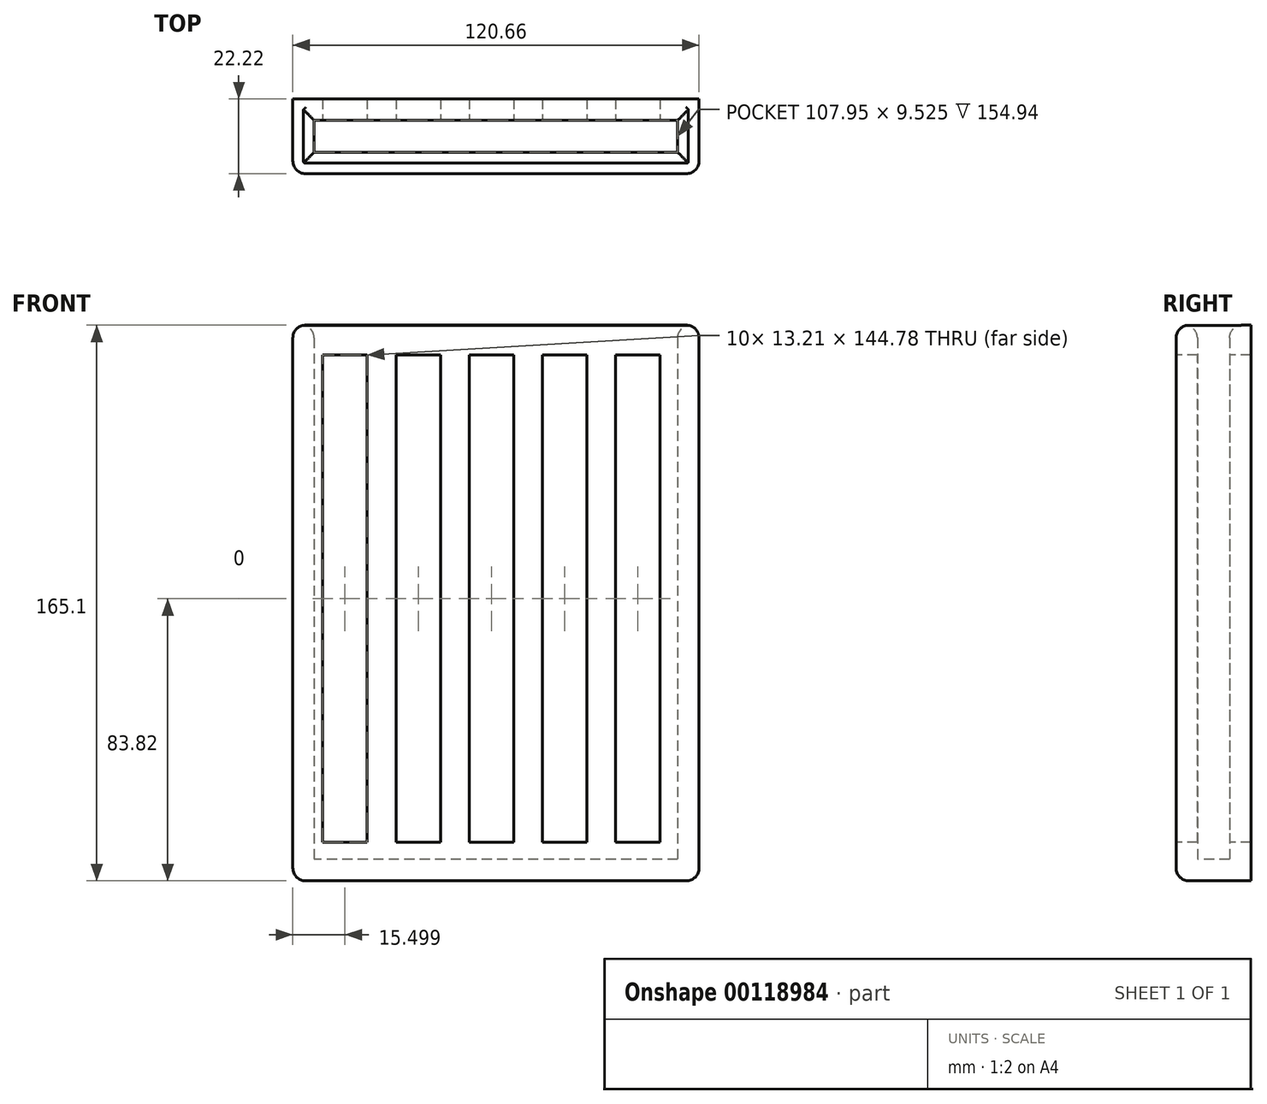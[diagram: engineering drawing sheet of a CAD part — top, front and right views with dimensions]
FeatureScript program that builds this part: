
annotation { "Feature Type Name" : "Feature", "Feature Type Description" : "" }
export const myFeature = defineFeature(function(context is Context, id is Id, definition is map)
    precondition{}
    {
        {
            var Q0;
            Q0=qCreatedBy(makeId("Top.planeOp"),FACE);
            var sketch = newSketch(context, id + "F0", { "sketchPlane" : qUnion([Q0])});
            skLineSegment(sketch, "E0", {"start": v(-60.33, 11.11) * mm, "end": v(60.33, 11.11) * mm});
            skLineSegment(sketch, "E1", {"start": v(60.33, 11.11) * mm, "end": v(60.33, -11.11) * mm});
            skLineSegment(sketch, "E2", {"start": v(60.33, -11.11) * mm, "end": v(-60.33, -11.11) * mm});
            skLineSegment(sketch, "E3", {"start": v(-60.33, -11.11) * mm, "end": v(-60.33, 11.11) * mm});
            skLineSegment(sketch, "E4", {"start": v(-53.98, 4.76) * mm, "end": v(-53.98, -4.76) * mm});
            skLineSegment(sketch, "E5", {"start": v(-53.98, -4.76) * mm, "end": v(53.98, -4.76) * mm});
            skLineSegment(sketch, "E6", {"start": v(53.98, -4.76) * mm, "end": v(53.98, 4.76) * mm});
            skLineSegment(sketch, "E7", {"start": v(53.98, 4.76) * mm, "end": v(-53.98, 4.76) * mm});
            skSolve(sketch);
        }
        {
            var Q0;
            Q0=makeQuery(id+"F0.imprint","IMPRINT",FACE,{"disambiguationData":[TD([[makeQuery(id+"F0.imprint","IMPRINT",EDGE,{"derivedFrom":sQuery(id+"F0.wireOp",EDGE,"E0")}),-1.0]])]});
            extrude(context, id + "F1", {"entities" : qUnion([Q0]), "depth" : 165.1 * mm});
        }
        {
            var Q0;
            Q0=qCreatedBy(makeId("Right.planeOp"),FACE);
            var sketch = newSketch(context, id + "F2", { "sketchPlane" : qUnion([Q0])});
            skLineSegment(sketch, "E8.bottom", {"start": v(-11.11, 6.35) * mm, "end": v(11.11, 6.35) * mm});
            skLineSegment(sketch, "E8.top", {"start": v(-11.11, 0) * mm, "end": v(11.11, 0) * mm});
            skLineSegment(sketch, "E8.left", {"start": v(-11.11, 6.35) * mm, "end": v(-11.11, 0) * mm});
            skLineSegment(sketch, "E8.right", {"start": v(11.11, 6.35) * mm, "end": v(11.11, 0) * mm});
            skSolve(sketch);
        }
        {
            var Q0;
            Q0 = qSketchRegion(id + "F2", true);
            extrude(context, id + "F3", {"entities" : qUnion([Q0]), "operationType" : NewBodyOperationType.ADD, "endBound" : BoundingType.SYMMETRIC, "depth" : 111.76 * mm});
        }
        {
            var Q0;
            Q0=makeQuery(id+"F1.opExtrude","SWEPT_FACE",FACE,{"disambiguationData":[OSD([sQuery(id+"F0.wireOp",EDGE,"E2")])]});
            var sketch = newSketch(context, id + "F4", { "sketchPlane" : qUnion([Q0])});
            skLineSegment(sketch, "E9.bottom", {"start": v(-51.44, 156.21) * mm, "end": v(-38.23, 156.21) * mm});
            skLineSegment(sketch, "E9.top", {"start": v(-51.44, 11.43) * mm, "end": v(-38.23, 11.43) * mm});
            skLineSegment(sketch, "E9.left", {"start": v(-51.44, 156.21) * mm, "end": v(-51.44, 11.43) * mm});
            skLineSegment(sketch, "E9.right", {"start": v(-38.23, 156.21) * mm, "end": v(-38.23, 11.43) * mm});
            skLineSegment(sketch, "E10.1.0.0", {"start": v(-29.7, 156.21) * mm, "end": v(-29.7, 11.43) * mm});
            skLineSegment(sketch, "E10.1.0.1", {"start": v(-29.7, 156.21) * mm, "end": v(-16.48, 156.21) * mm});
            skLineSegment(sketch, "E10.1.0.2", {"start": v(-16.48, 156.21) * mm, "end": v(-16.48, 11.43) * mm});
            skLineSegment(sketch, "E10.1.0.3", {"start": v(-29.7, 11.43) * mm, "end": v(-16.48, 11.43) * mm});
            skLineSegment(sketch, "E10.2.0.0", {"start": v(-7.95, 156.21) * mm, "end": v(-7.95, 11.43) * mm});
            skLineSegment(sketch, "E10.2.0.1", {"start": v(-7.95, 156.21) * mm, "end": v(5.26, 156.21) * mm});
            skLineSegment(sketch, "E10.2.0.2", {"start": v(5.26, 156.21) * mm, "end": v(5.26, 11.43) * mm});
            skLineSegment(sketch, "E10.2.0.3", {"start": v(-7.95, 11.43) * mm, "end": v(5.26, 11.43) * mm});
            skLineSegment(sketch, "E10.3.0.0", {"start": v(13.8, 156.21) * mm, "end": v(13.8, 11.43) * mm});
            skLineSegment(sketch, "E10.3.0.1", {"start": v(13.8, 156.21) * mm, "end": v(27, 156.21) * mm});
            skLineSegment(sketch, "E10.3.0.2", {"start": v(27, 156.21) * mm, "end": v(27, 11.43) * mm});
            skLineSegment(sketch, "E10.3.0.3", {"start": v(13.8, 11.43) * mm, "end": v(27, 11.43) * mm});
            skLineSegment(sketch, "E10.4.0.0", {"start": v(35.53, 156.21) * mm, "end": v(35.53, 11.43) * mm});
            skLineSegment(sketch, "E10.4.0.1", {"start": v(35.53, 156.21) * mm, "end": v(48.74, 156.21) * mm});
            skLineSegment(sketch, "E10.4.0.2", {"start": v(48.74, 156.21) * mm, "end": v(48.74, 11.43) * mm});
            skLineSegment(sketch, "E10.4.0.3", {"start": v(35.53, 11.43) * mm, "end": v(48.74, 11.43) * mm});
            skLineSegment(sketch, "E10.direction1", {"start": v(-51.44, 11.43) * mm, "end": v(-29.7, 11.43) * mm, "construction": true});
            skSolve(sketch);
        }
        {
            var Q0;
            Q0=makeQuery(id+"F1.opExtrude","CAP_EDGE",EDGE,{"disambiguationData":[OSD([sQuery(id+"F0.wireOp",EDGE,"E2")])],"isStart":false});
            var Q1;
            Q1=makeQuery(id+"F1.opExtrude","CAP_EDGE",EDGE,{"disambiguationData":[OSD([sQuery(id+"F0.wireOp",EDGE,"E3")])],"isStart":false});
            var Q2;
            Q2=makeQuery(id+"F1.opExtrude","CAP_EDGE",EDGE,{"disambiguationData":[OSD([sQuery(id+"F0.wireOp",EDGE,"E1")])],"isStart":false});
            var Q3;
            Q3=makeQuery(id+"F1.opExtrude","SWEPT_EDGE",EDGE,{"disambiguationData":[OSD([sQuery(id+"F0.wireOp",EDGE,"E1"),sQuery(id+"F0.wireOp",EDGE,"E2")])]});
            var Q4;
            Q4=makeQuery(id+"F1.opExtrude","SWEPT_EDGE",EDGE,{"disambiguationData":[OSD([sQuery(id+"F0.wireOp",EDGE,"E2"),sQuery(id+"F0.wireOp",EDGE,"E3")])]});
            var Q5;
            Q5=makeQuery(id+"F1.opExtrude","CAP_EDGE",EDGE,{"disambiguationData":[OSD([sQuery(id+"F0.wireOp",EDGE,"E2")])],"isStart":true});
            var Q6;
            Q6=makeQuery(id+"F1.opExtrude","CAP_EDGE",EDGE,{"disambiguationData":[OSD([sQuery(id+"F0.wireOp",EDGE,"E1")])],"isStart":true});
            var Q7;
            Q7=makeQuery(id+"F1.opExtrude","CAP_EDGE",EDGE,{"disambiguationData":[OSD([sQuery(id+"F0.wireOp",EDGE,"E3")])],"isStart":true});
            var Q8;
            Q8=makeQuery(id+"F1.opExtrude","CAP_EDGE",EDGE,{"disambiguationData":[OSD([sQuery(id+"F0.wireOp",EDGE,"E6")])],"isStart":false});
            var Q9;
            Q9=makeQuery(id+"F1.opExtrude","CAP_EDGE",EDGE,{"disambiguationData":[OSD([sQuery(id+"F0.wireOp",EDGE,"E5")])],"isStart":false});
            var Q10;
            Q10=makeQuery(id+"F1.opExtrude","CAP_EDGE",EDGE,{"disambiguationData":[OSD([sQuery(id+"F0.wireOp",EDGE,"E4")])],"isStart":false});
            var Q11;
            Q11=makeQuery(id+"F1.opExtrude","CAP_EDGE",EDGE,{"disambiguationData":[OSD([sQuery(id+"F0.wireOp",EDGE,"E7")])],"isStart":false});
            fillet(context, id + "F5", {"entities" : qUnion([Q0, Q1, Q2, Q3, Q4, Q5, Q6, Q7, Q8, Q9, Q10, Q11]), "radius" : 3.8 * mm, "tangentPropagation" : true, "allowEdgeOverflow" : false});
        }
        {
            var Q0;
            Q0=makeQuery(id+"F4.imprint","IMPRINT",FACE,{"disambiguationData":[TD([[makeQuery(id+"F4.imprint","IMPRINT",EDGE,{"derivedFrom":sQuery(id+"F4.wireOp",EDGE,"E9.bottom")}),-1.0]])]});
            var Q1;
            Q1=makeQuery(id+"F4.imprint","IMPRINT",FACE,{"disambiguationData":[TD([[makeQuery(id+"F4.imprint","IMPRINT",EDGE,{"derivedFrom":sQuery(id+"F4.wireOp",EDGE,"E10.1.0.0")}),1.0]])]});
            var Q2;
            Q2=makeQuery(id+"F4.imprint","IMPRINT",FACE,{"disambiguationData":[TD([[makeQuery(id+"F4.imprint","IMPRINT",EDGE,{"derivedFrom":sQuery(id+"F4.wireOp",EDGE,"E10.2.0.0")}),1.0]])]});
            var Q3;
            Q3=makeQuery(id+"F4.imprint","IMPRINT",FACE,{"disambiguationData":[TD([[makeQuery(id+"F4.imprint","IMPRINT",EDGE,{"derivedFrom":sQuery(id+"F4.wireOp",EDGE,"E10.3.0.0")}),1.0]])]});
            var Q4;
            Q4=makeQuery(id+"F4.imprint","IMPRINT",FACE,{"disambiguationData":[TD([[makeQuery(id+"F4.imprint","IMPRINT",EDGE,{"derivedFrom":sQuery(id+"F4.wireOp",EDGE,"E10.4.0.0")}),1.0]])]});
            var Q5;
            Q5=makeQuery(id+"F4.imprint","IMPRINT",FACE,{"disambiguationData":[TD([[makeQuery(id+"F4.imprint","IMPRINT",EDGE,{"derivedFrom":sQuery(id+"F4.wireOp",EDGE,"E10.5.0.0")}),1.0]])]});
            extrude(context, id + "F6", {"entities" : qUnion([Q0, Q1, Q2, Q3, Q4, Q5]), "operationType" : NewBodyOperationType.REMOVE, "oppositeDirection" : true, "depth" : 40.64 * mm});
        }
    });
